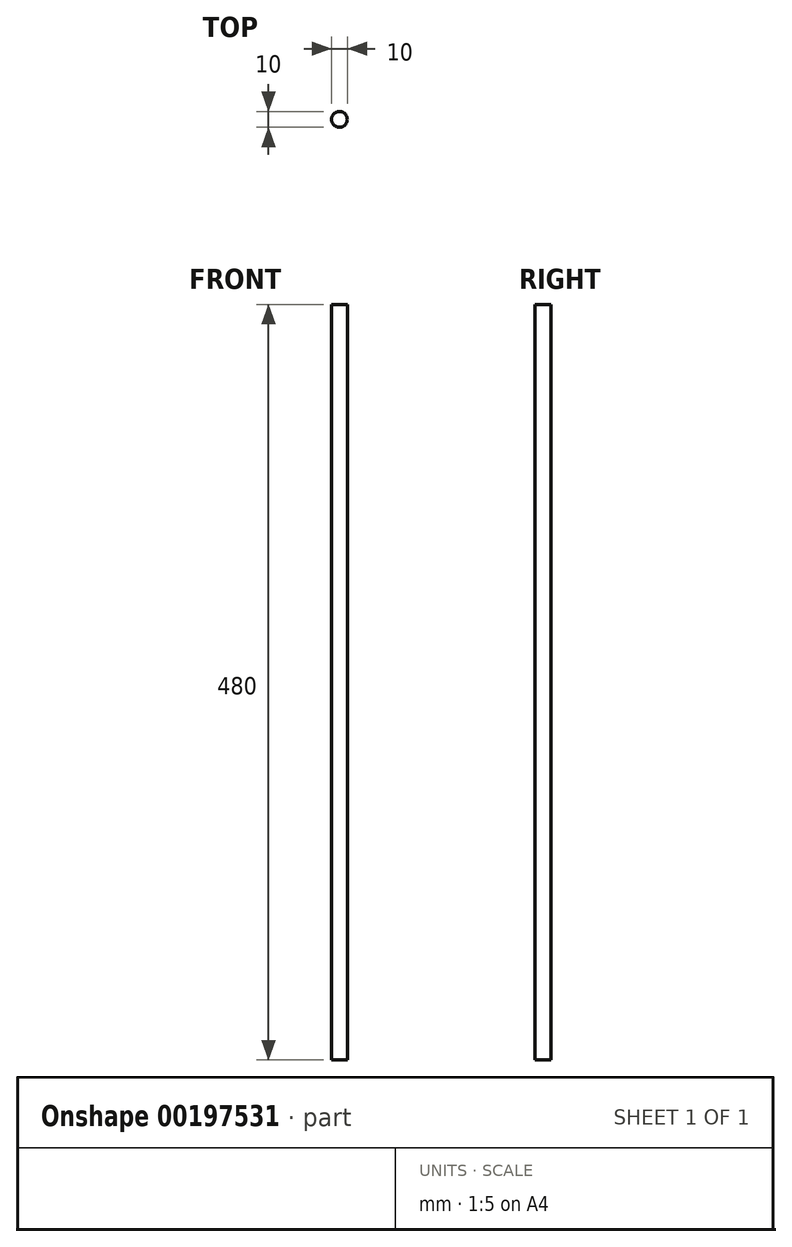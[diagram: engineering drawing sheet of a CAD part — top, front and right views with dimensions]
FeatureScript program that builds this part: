
annotation { "Feature Type Name" : "Feature", "Feature Type Description" : "" }
export const myFeature = defineFeature(function(context is Context, id is Id, definition is map)
    precondition{}
    {
        {
            var Q0;
            Q0=qCreatedBy(makeId("Top.planeOp"),FACE);
            var sketch = newSketch(context, id + "F0", { "sketchPlane" : qUnion([Q0])});
            skCircle(sketch, "E0", {"center": v(0, 0) * mm, "radius": 5 * mm});
            skSolve(sketch);
        }
        {
            var Q0;
            Q0=qSketchRegion(id+"F0",true);
            extrude(context, id + "F1", {"entities" : qUnion([Q0]), "depth" : 480 * mm});
        }
    });
